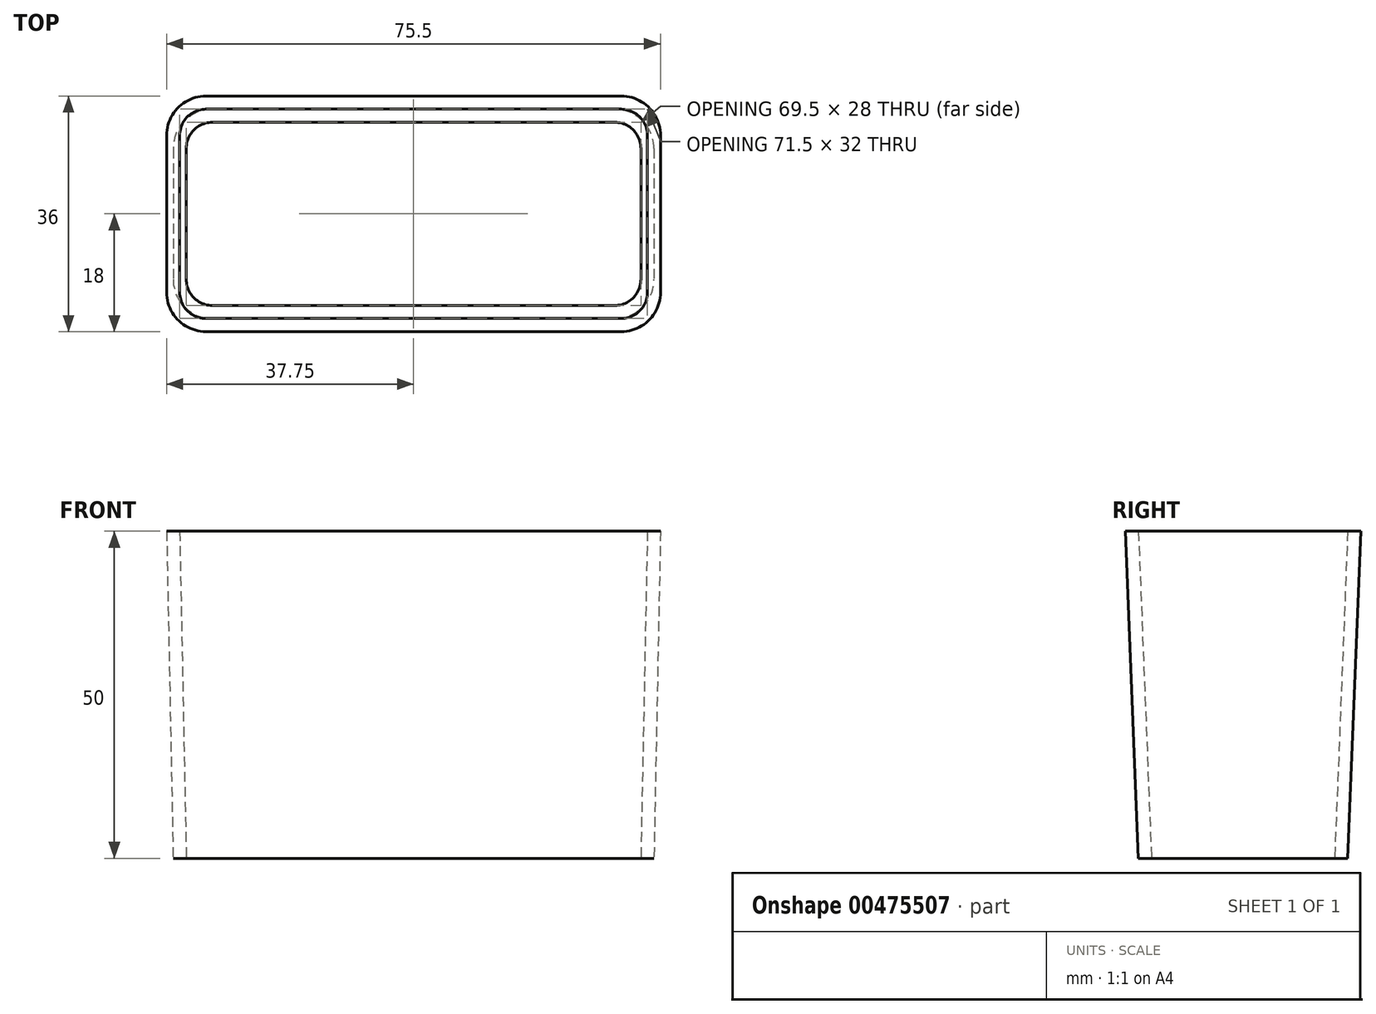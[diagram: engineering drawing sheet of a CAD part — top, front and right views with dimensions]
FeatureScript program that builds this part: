
annotation { "Feature Type Name" : "Feature", "Feature Type Description" : "" }
export const myFeature = defineFeature(function(context is Context, id is Id, definition is map)
    precondition{}
    {
        {
            var Q0;
            Q0=qCreatedBy(makeId("Top.planeOp"),FACE);
            var sketch = newSketch(context, id + "F0", { "sketchPlane" : qUnion([Q0])});
            skLineSegment(sketch, "E0.bottom", {"start": v(-31.75, 16) * mm, "end": v(31.75, 16) * mm});
            skLineSegment(sketch, "E0.top", {"start": v(-31.75, -16) * mm, "end": v(31.75, -16) * mm});
            skLineSegment(sketch, "E0.left", {"start": v(-35.75, 12) * mm, "end": v(-35.75, -12) * mm});
            skLineSegment(sketch, "E0.right", {"start": v(35.75, 12) * mm, "end": v(35.75, -12) * mm});
            skPoint(sketch, "E1.visualSharp", {"position": v(-35.75, 16) * mm});
            skArc(sketch, "E1.filletArc", {"start": v(-31.75, 16) * mm, "mid": v(-34.58, 14.83) * mm, "end": v(-35.75, 12) * mm});
            skPoint(sketch, "E2.visualSharp", {"position": v(35.75, 16) * mm});
            skArc(sketch, "E2.filletArc", {"start": v(35.75, 12) * mm, "mid": v(34.58, 14.83) * mm, "end": v(31.75, 16) * mm});
            skPoint(sketch, "E3.visualSharp", {"position": v(35.75, -16) * mm});
            skArc(sketch, "E3.filletArc", {"start": v(31.75, -16) * mm, "mid": v(34.58, -14.83) * mm, "end": v(35.75, -12) * mm});
            skPoint(sketch, "E4.visualSharp", {"position": v(-35.75, -16) * mm});
            skArc(sketch, "E4.filletArc", {"start": v(-35.75, -12) * mm, "mid": v(-34.58, -14.83) * mm, "end": v(-31.75, -16) * mm});
            skSolve(sketch);
        }
        {
            var Q0;
            Q0=qCreatedBy(makeId("Top.planeOp"),FACE);
            cPlane(context, id + "F1", {"entities" : qUnion([Q0]), "cplaneType" : CPlaneType.OFFSET, "offset" : 50 * mm, "oppositeDirection" : true, "width" : 150 * mm, "height" : 150 * mm});
        }
        {
            var Q0;
            Q0=qCreatedBy(id+"F1.planeOp",FACE);
            var sketch = newSketch(context, id + "F2", { "sketchPlane" : qUnion([Q0])});
            skLineSegment(sketch, "E5.bottom", {"start": v(-30.75, 14) * mm, "end": v(30.75, 14) * mm});
            skLineSegment(sketch, "E5.top", {"start": v(-30.75, -14) * mm, "end": v(30.75, -14) * mm});
            skLineSegment(sketch, "E5.left", {"start": v(-34.75, 10) * mm, "end": v(-34.75, -10) * mm});
            skLineSegment(sketch, "E5.right", {"start": v(34.75, 10) * mm, "end": v(34.75, -10) * mm});
            skArc(sketch, "E6.filletArc", {"start": v(-30.75, 14) * mm, "mid": v(-33.58, 12.83) * mm, "end": v(-34.75, 10) * mm});
            skPoint(sketch, "E7.visualSharp", {"position": v(34.75, 14) * mm});
            skArc(sketch, "E7.filletArc", {"start": v(34.75, 10) * mm, "mid": v(33.58, 12.83) * mm, "end": v(30.75, 14) * mm});
            skPoint(sketch, "E8.visualSharp", {"position": v(34.75, -14) * mm});
            skArc(sketch, "E8.filletArc", {"start": v(30.75, -14) * mm, "mid": v(33.58, -12.83) * mm, "end": v(34.75, -10) * mm});
            skPoint(sketch, "E9.visualSharp", {"position": v(-34.75, -14) * mm});
            skArc(sketch, "E9.filletArc", {"start": v(-34.75, -10) * mm, "mid": v(-33.58, -12.83) * mm, "end": v(-30.75, -14) * mm});
            skSolve(sketch);
        }
        {
            var Q0;
            Q0=qCreatedBy(makeId("Top.planeOp"),FACE);
            var sketch = newSketch(context, id + "F3", { "sketchPlane" : qUnion([Q0])});
            skPoint(sketch, "E10.visualSharp", {"position": v(-35.75, 16) * mm});
            skPoint(sketch, "E11.visualSharp", {"position": v(35.75, 16) * mm});
            skPoint(sketch, "E12.visualSharp", {"position": v(35.75, -16) * mm});
            skPoint(sketch, "E13.visualSharp", {"position": v(-35.75, -16) * mm});
            skArc(sketch, "E14.0", {"start": v(-31.75, 18) * mm, "mid": v(-36, 16.24) * mm, "end": v(-37.75, 12) * mm});
            skLineSegment(sketch, "E14.1", {"start": v(-37.75, 12) * mm, "end": v(-37.75, -12) * mm});
            skLineSegment(sketch, "E14.2", {"start": v(-31.75, 18) * mm, "end": v(31.75, 18) * mm});
            skArc(sketch, "E14.3", {"start": v(-37.75, -12) * mm, "mid": v(-36, -16.24) * mm, "end": v(-31.75, -18) * mm});
            skArc(sketch, "E14.4", {"start": v(37.75, 12) * mm, "mid": v(36, 16.24) * mm, "end": v(31.75, 18) * mm});
            skLineSegment(sketch, "E14.5", {"start": v(37.75, 12) * mm, "end": v(37.75, -12) * mm});
            skArc(sketch, "E14.6", {"start": v(31.75, -18) * mm, "mid": v(36, -16.24) * mm, "end": v(37.75, -12) * mm});
            skLineSegment(sketch, "E14.7", {"start": v(-31.75, -18) * mm, "end": v(31.75, -18) * mm});
            skSolve(sketch);
        }
        {
            var Q0;
            Q0=qCreatedBy(id+"F1.planeOp",FACE);
            var sketch = newSketch(context, id + "F4", { "sketchPlane" : qUnion([Q0])});
            skPoint(sketch, "E15.visualSharp", {"position": v(-34.75, 14) * mm});
            skPoint(sketch, "E16.visualSharp", {"position": v(34.75, 14) * mm});
            skPoint(sketch, "E17.visualSharp", {"position": v(34.75, -14) * mm});
            skPoint(sketch, "E18.visualSharp", {"position": v(-34.75, -14) * mm});
            skArc(sketch, "E19.0", {"start": v(-30.75, 16) * mm, "mid": v(-35, 14.24) * mm, "end": v(-36.75, 10) * mm});
            skLineSegment(sketch, "E19.1", {"start": v(-36.75, 10) * mm, "end": v(-36.75, -10) * mm});
            skLineSegment(sketch, "E19.2", {"start": v(-30.75, 16) * mm, "end": v(30.75, 16) * mm});
            skArc(sketch, "E19.3", {"start": v(-36.75, -10) * mm, "mid": v(-35, -14.24) * mm, "end": v(-30.75, -16) * mm});
            skArc(sketch, "E19.4", {"start": v(36.75, 10) * mm, "mid": v(35, 14.24) * mm, "end": v(30.75, 16) * mm});
            skLineSegment(sketch, "E19.5", {"start": v(36.75, 10) * mm, "end": v(36.75, -10) * mm});
            skArc(sketch, "E19.6", {"start": v(30.75, -16) * mm, "mid": v(35, -14.24) * mm, "end": v(36.75, -10) * mm});
            skLineSegment(sketch, "E19.7", {"start": v(-30.75, -16) * mm, "end": v(30.75, -16) * mm});
            skSolve(sketch);
        }
        {
            var Q0;
            Q0=makeQuery(id+"F3.imprint","IMPRINT",FACE,{"disambiguationData":[TD([[makeQuery(id+"F3.imprint","IMPRINT",EDGE,{"derivedFrom":sQuery(id+"F3.wireOp",EDGE,"E14.0")}),1.0]])]});
            var Q1;
            Q1=makeQuery(id+"F4.imprint","IMPRINT",FACE,{"disambiguationData":[TD([[makeQuery(id+"F4.imprint","IMPRINT",EDGE,{"derivedFrom":sQuery(id+"F4.wireOp",EDGE,"E19.0")}),1.0]])]});
            loft(context, id + "F5", {"sheetProfilesArray" : [{ "sheetProfileEntities" : qUnion([Q0]) }, { "sheetProfileEntities" : qUnion([Q1]) }]});
        }
        {
            var Q1;
            Q1 = qSketchRegion(id + "F0", true);
            var Q2;
            Q2 = qSketchRegion(id + "F2", true);
            loft(context, id + "F6", {"operationType" : NewBodyOperationType.REMOVE, "sheetProfilesArray" : [{ "sheetProfileEntities" : qUnion([Q1]) }, { "sheetProfileEntities" : qUnion([Q2]) }]});
        }
    });
